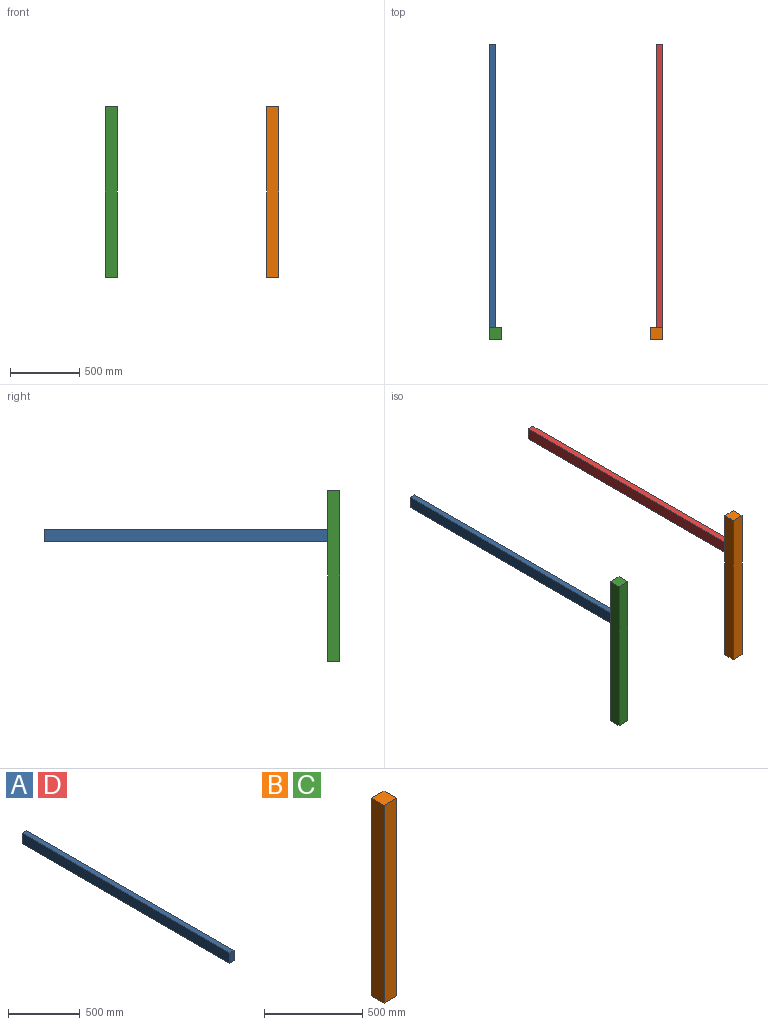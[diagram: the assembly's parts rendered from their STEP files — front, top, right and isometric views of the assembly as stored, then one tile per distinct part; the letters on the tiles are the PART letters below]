
ASSEMBLY  parts=4 mates=7
PART A: 6 faces, bbox 44.5x2051.1x88.9 mm
  f0: plane 2051.05x44.45mm, normal (0,0,-1), area 91169.2mm2, adj f1,f3,f4,f5
  f1: plane 88.9x44.45mm, normal (0,1,0), area 3951.6mm2, adj f0,f2,f4,f5
  f2: plane 2051.05x44.45mm, normal (0,0,1), area 91169.2mm2, adj f1,f3,f4,f5
  f3: plane 88.9x44.45mm, normal (0,-1,0), area 3951.6mm2, adj f0,f2,f4,f5
  f4: plane 2051.05x88.9mm, normal (1,0,0), area 182338.3mm2, adj f0,f1,f2,f3
  f5: plane 2051.05x88.9mm, normal (-1,0,0), area 182338.3mm2, adj f0,f1,f2,f3
PART B: 6 faces, bbox 88.9x88.9x1231.9 mm
  f0: plane 1231.9x88.9mm, normal (1,0,0), area 109515.9mm2, adj f1,f3,f4,f5
  f1: plane 1231.9x88.9mm, normal (0,1,0), area 109515.9mm2, adj f0,f2,f4,f5
  f2: plane 1231.9x88.9mm, normal (-1,0,0), area 109515.9mm2, adj f1,f3,f4,f5
  f3: plane 1231.9x88.9mm, normal (0,-1,0), area 109515.9mm2, adj f0,f2,f4,f5
  f4: plane 88.9x88.9mm, normal (0,0,1), area 7903.2mm2, adj f0,f1,f2,f3
  f5: plane 88.9x88.9mm, normal (0,0,-1), area 7903.2mm2, adj f0,f1,f2,f3
PART C: same geometry as B
PART D: same geometry as A
PLACE A t=(-1191.68,443.77,1439.27)mm
PLACE B t=(67.64,-219.07,292.54)mm
PLACE C t=(-1102.78,-219.07,292.54)mm
PLACE D t=(23.19,443.77,1439.27)mm
MATE planar C.f4 <-> B.f4  axis (0,0,1) through (-1147.23,-174.62,1524.44)mm
MATE planar C.f3 <-> B.f3  axis (0,-1,0) through (-1147.23,-219.07,908.49)mm
MATE planar D.f4 <-> B.f0  axis (1,0,0) through (67.64,-130.17,1201.97)mm
MATE planar D.f3 <-> B.f1  axis (0,-1,0) through (45.42,-130.17,1201.97)mm
MATE planar A.f0 <-> D.f0  axis (0,0,-1) through (-1169.46,895.35,1157.52)mm
MATE planar A.f5 <-> C.f2  axis (-1,0,0) through (-1191.68,895.35,1201.97)mm
MATE planar C.f1 <-> A.f3  axis (0,1,0) through (-1147.23,-130.17,908.49)mm
